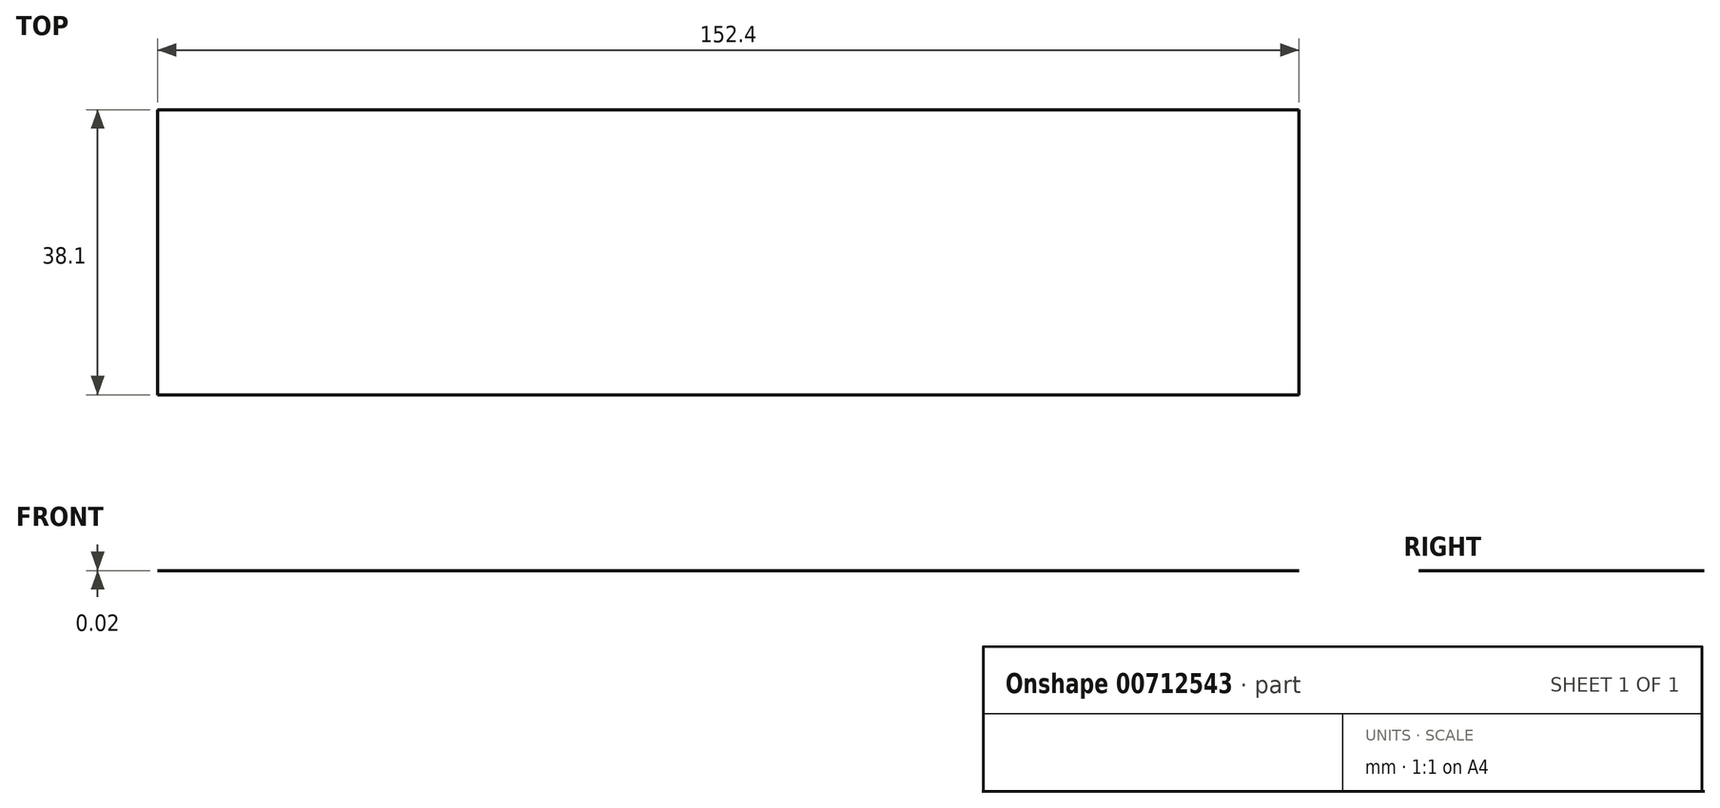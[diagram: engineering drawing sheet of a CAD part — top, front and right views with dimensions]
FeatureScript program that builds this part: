
annotation { "Feature Type Name" : "Feature", "Feature Type Description" : "" }
export const myFeature = defineFeature(function(context is Context, id is Id, definition is map)
    precondition{}
    {
        {
            var Q0;
            Q0=qCreatedBy(makeId("Top.planeOp"),FACE);
            var sketch = newSketch(context, id + "F0", { "sketchPlane" : qUnion([Q0])});
            skLineSegment(sketch, "E0.bottom", {"start": v(76.2, -19.05) * mm, "end": v(-76.2, -19.05) * mm});
            skLineSegment(sketch, "E0.top", {"start": v(76.2, 19.05) * mm, "end": v(-76.2, 19.05) * mm});
            skLineSegment(sketch, "E0.left", {"start": v(76.2, -19.05) * mm, "end": v(76.2, 19.05) * mm});
            skLineSegment(sketch, "E0.right", {"start": v(-76.2, -19.05) * mm, "end": v(-76.2, 19.05) * mm});
            skPoint(sketch, "E0.middle", {"position": v(0, 0) * mm});
            skSolve(sketch);
        }
        {
            var Q0;
            Q0 = qSketchRegion(id + "F0", true);
            extrude(context, id + "F1", {"entities" : qUnion([Q0]), "depth" : 5 / 203.2 * mm, "offsetDistance" : 25.4 * mm});
        }
    });
